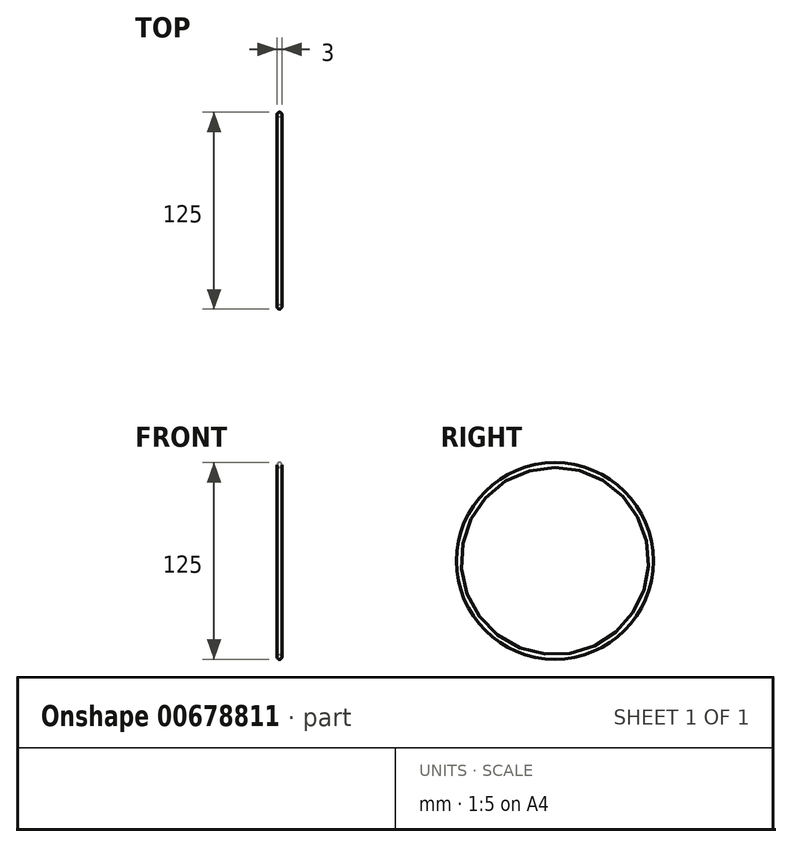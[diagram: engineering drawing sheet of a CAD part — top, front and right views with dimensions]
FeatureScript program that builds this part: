
annotation { "Feature Type Name" : "Feature", "Feature Type Description" : "" }
export const myFeature = defineFeature(function(context is Context, id is Id, definition is map)
    precondition{}
    {
        {
            var Q0;
            Q0=qCreatedBy(makeId("Front.planeOp"),FACE);
            var sketch = newSketch(context, id + "F0", { "sketchPlane" : qUnion([Q0])});
            skCircle(sketch, "E0", {"center": v(0, 61) * mm, "radius": 1.5 * mm});
            skSolve(sketch);
        }
        {
            var Q0;
            Q0=qCreatedBy(makeId("Front.planeOp"),FACE);
            var sketch = newSketch(context, id + "F1", { "sketchPlane" : qUnion([Q0])});
            skLineSegment(sketch, "E1", {"start": v(-30.15, 0) * mm, "end": v(34.83, 0) * mm});
            skSolve(sketch);
        }
        {
            var Q0;
            Q0=makeQuery(id+"F0.imprint","IMPRINT",FACE,{"disambiguationData":[TD([[makeQuery(id+"F0.imprint","IMPRINT",EDGE,{"derivedFrom":sQuery(id+"F0.wireOp",EDGE,"E0")}),1.0]])]});
            var Q1;
            Q1=sQuery(id+"F1.wireOp",EDGE,"E1");
            revolve(context, id + "F2", {"entities" : qUnion([Q0]), "axis" : qUnion([Q1]), "revolveType" : RevolveType.FULL});
        }
    });
